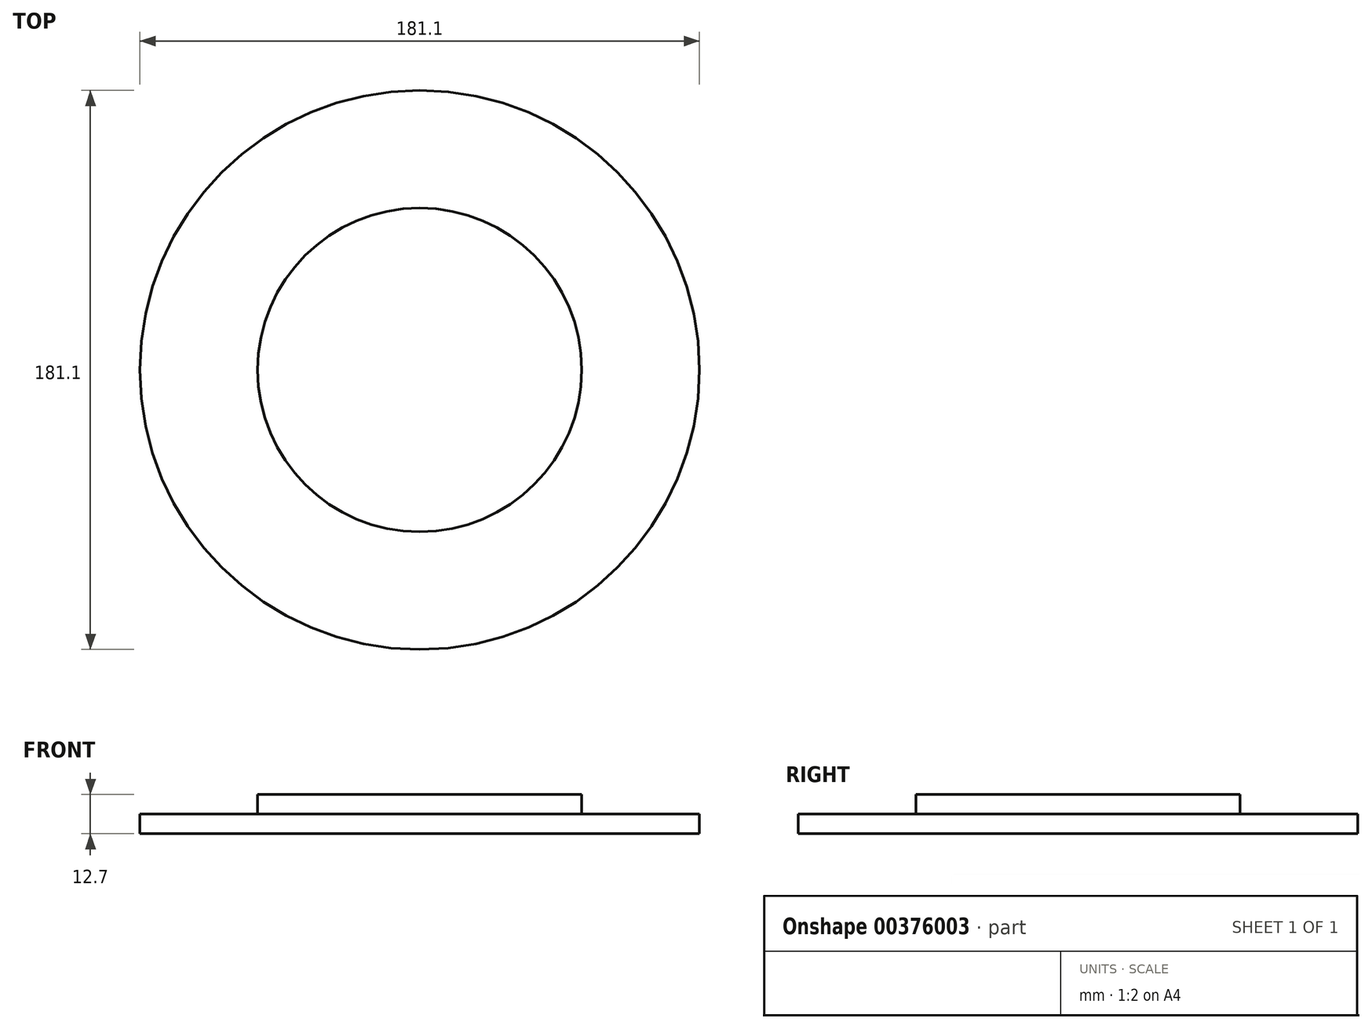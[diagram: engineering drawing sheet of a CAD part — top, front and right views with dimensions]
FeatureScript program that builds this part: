
annotation { "Feature Type Name" : "Feature", "Feature Type Description" : "" }
export const myFeature = defineFeature(function(context is Context, id is Id, definition is map)
    precondition{}
    {
        {
            var Q0;
            Q0=qCreatedBy(makeId("Front.planeOp"),FACE);
            var sketch = newSketch(context, id + "F0", { "sketchPlane" : qUnion([Q0])});
            skLineSegment(sketch, "E0", {"start": v(0, 0) * mm, "end": v(-90.55, 0) * mm});
            skLineSegment(sketch, "E1", {"start": v(-90.55, 0) * mm, "end": v(-90.55, 6.35) * mm});
            skLineSegment(sketch, "E2", {"start": v(-90.55, 6.35) * mm, "end": v(-52.45, 6.35) * mm});
            skLineSegment(sketch, "E3", {"start": v(-52.45, 6.35) * mm, "end": v(-52.45, 12.7) * mm});
            skLineSegment(sketch, "E4", {"start": v(-52.45, 12.7) * mm, "end": v(0, 12.7) * mm});
            skLineSegment(sketch, "E5", {"start": v(0, 12.7) * mm, "end": v(0, 0) * mm});
            skSolve(sketch);
        }
        {
            var Q0;
            Q0=makeQuery(id+"F0.imprint","IMPRINT",FACE,{"disambiguationData":[TD([[makeQuery(id+"F0.imprint","IMPRINT",EDGE,{"derivedFrom":sQuery(id+"F0.wireOp",EDGE,"E0")}),-1.0]])]});
            var Q1;
            Q1=sQuery(id+"F0.wireOp",EDGE,"E5");
            revolve(context, id + "F1", {"entities" : qUnion([Q0]), "axis" : qUnion([Q1]), "revolveType" : RevolveType.FULL});
        }
    });
